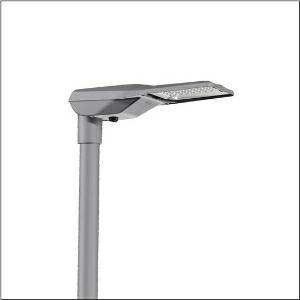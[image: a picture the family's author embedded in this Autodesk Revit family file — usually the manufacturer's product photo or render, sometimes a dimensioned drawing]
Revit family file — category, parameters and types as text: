
# Revit family: streetlight_sl_21_iq_mini___st1_0ab_5xe2m31u08gb_fb61
name_source: partatom
category: Lighting Fixtures
units: mm (PartAtom-declared; Revit-internal decimal feet)

## family parameters
Cut with Voids When Loaded = No
Host = Face
Light Source = No
Part Type = Normal
Room Calculation Point = No
Round Connector Dimension = Use Diameter
Shared = No

## types (1)
- --- (1 x LED, 5270 lm, 39.8 W, 3000K)
    Apparent Load = 40 VA
    CIE Flux Codes = 38 73 97 100 100
    Color Rendering = 70
    Color Temperature = 3000K
    Default Elevation = 1800 mm
    Description = Streetlight SL 21 iQ mini, mast luminaire, primary light control with lens, of PMMA, primary optical cover: cover, of toughened safety glass, transparent, light distribution: ST1.0aB, light emission: direct distribution, primary light characteristic: asymmetric, installation type: post-top, side-entry, LED, High Power LED, rated luminous flux: 5.270lm, luminous efficacy: 132lm/W, light colour: 730, colour temperature: 3000K, control gear: iQ-Street Remote, D4i with power reduction, control: pre-setting: logarithmic dimming characteristic, Street-Remote, Auto-Match, Temp-Guard, Lumen-Switch, Night-Set, Smart-Wire, Light-Fading, Desk-Remote (wireless, voltage-free reading and setting of iQ features in the workshop via application-optimized NFC function/RFID function), optimised constant luminous flux control (CLO 2.0), mains connection: 220..240V, AC, 50/60Hz, start of lifetime: 40W, end of service life: 41W, reduction: 18W, luminaire housing, of diecast aluminium, powder-coated, SITECO metallic grey (DB 702S), corrosivity category C5 high according to DIN EN ISO 12944, please order mast flange separately, inclination adjustable: 0°, 5°, 10°, 15°, sealing non-destructively replaceable, multi-level sealing system, length: 628mm, width: 235mm, height: 110mm, mast flange for spigot size: 42mm (side-entry): 5XC10008XM4, 60/48mm (side-entry/post-top): 5XC10108XM2, 76/60mm (side-entry/post-top): 5XC10108XM1, mounting height: 4..8m, Smart Interface below, protection rating (complete): IP66, insulation class (complete): insulation class II (safety insulation), certification: CE, ENEC, ENEC+, VDE, impact resistance: IK10, permissible operating ambient temperature for outdoor applications: -40..+50°C, standard-compliant lighting for roads and squares, packaging unit: 1 piece

Light Distribution: ST1.0aB
    Height = 110 mm
    Lamp = 1 x LED
    Lamp Light Flux = 5270 lm
    Lamp Power = 39.8 W
    Lamp count = 1
    Length = 625 mm
    Luminous efficacy = 132 lm/W
    Manufacturer = Siteco
    ModVariant = No
    Model = 5XE2M31U08GB
    Number of Poles = 1
    OnlyDefault = Yes
    Power Factor = 1
    Product Name = Streetlight SL 21 iQ mini | ST1.0aB
    Product group = mast luminaire | pylon top
    ProductGroupID = 6100
    Protection Class = Protection class II
    Protection Degree = IP 66
    RLX_Detail_Level = 1
    RLX_Emergency_Light_Flux = 0 lm
    RLX_Emergency_Type = 0
    RLX_Emergency_Type_DB = No
    RlxData = <blob elided: 93113 chars, md5=c2dd23f7>
    Socket = socket
    Standby Power = 0 W
    System Light Flux = 5270 lm
    System Power = 40 W
    Type Comments = factory setting: luminous flux: 100 % | dim-lin: 254 | 800 mA
    Type Image = l_1003516.jpg
    URL = http://relux.com
    VarID = @adj_112585
    Voltage = 0 V
    Weight = 0.00 kg
    Width = 234 mm

## geometry (parser evidence)
native form markers: Blend x4, Sweep x11
no freeform markers — native parametric forms only
